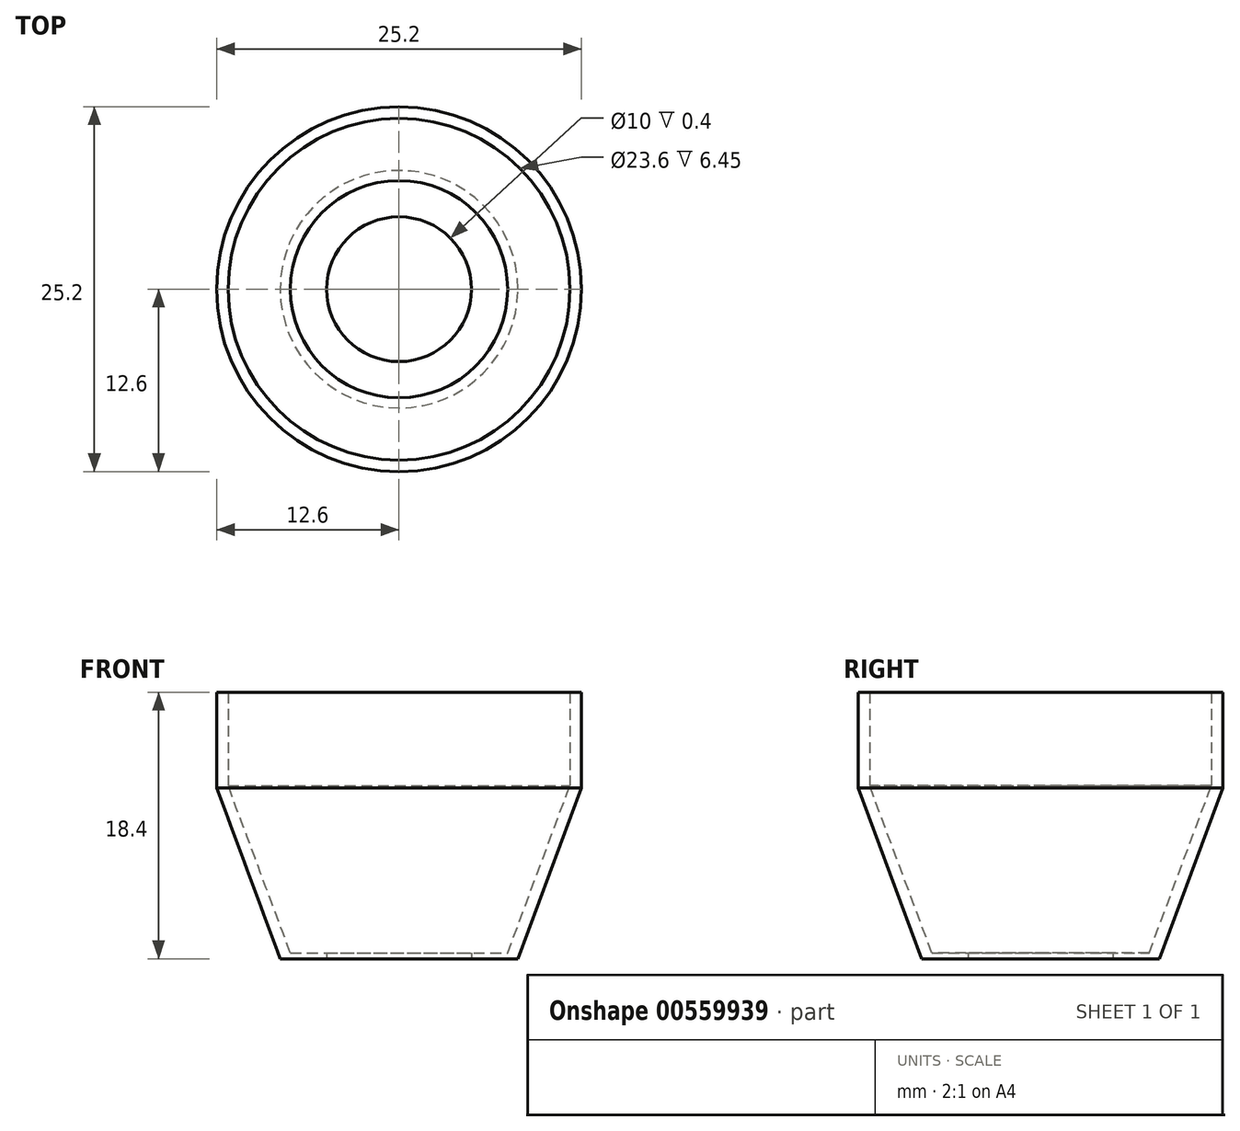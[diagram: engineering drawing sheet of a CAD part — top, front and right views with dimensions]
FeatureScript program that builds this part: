
annotation { "Feature Type Name" : "Feature", "Feature Type Description" : "" }
export const myFeature = defineFeature(function(context is Context, id is Id, definition is map)
    precondition{}
    {
        {
            var Q0;
            Q0=qCreatedBy(makeId("Front.planeOp"),FACE);
            var sketch = newSketch(context, id + "F0", { "sketchPlane" : qUnion([Q0])});
            skLineSegment(sketch, "E0", {"start": v(-5, -0.4) * mm, "end": v(-5, 0) * mm});
            skLineSegment(sketch, "E1", {"start": v(-5, 0) * mm, "end": v(-7.5, 0) * mm});
            skLineSegment(sketch, "E2", {"start": v(-7.5, 0) * mm, "end": v(-11.8, 11.55) * mm});
            skLineSegment(sketch, "E3", {"start": v(-11.8, 11.55) * mm, "end": v(-11.8, 18) * mm});
            skLineSegment(sketch, "E4.0", {"start": v(-12.6, 11.4) * mm, "end": v(-12.6, 18) * mm});
            skLineSegment(sketch, "E4.1", {"start": v(-8.2, -0.4) * mm, "end": v(-12.6, 11.4) * mm});
            skLineSegment(sketch, "E5", {"start": v(-5, -0.4) * mm, "end": v(-8.2, -0.4) * mm});
            skLineSegment(sketch, "E6", {"start": v(-12.6, 18) * mm, "end": v(-11.8, 18) * mm});
            skLineSegment(sketch, "E7", {"start": v(0, 0) * mm, "end": v(0, 19.9) * mm, "construction": true});
            skSolve(sketch);
        }
        {
            var Q0;
            Q0 = qSketchRegion(id + "F0", true);
            var Q1;
            Q1=sQuery(id+"F0.wireOp",EDGE,"E7");
            revolve(context, id + "F1", {"entities" : qUnion([Q0]), "axis" : qUnion([Q1]), "revolveType" : RevolveType.FULL});
        }
    });
